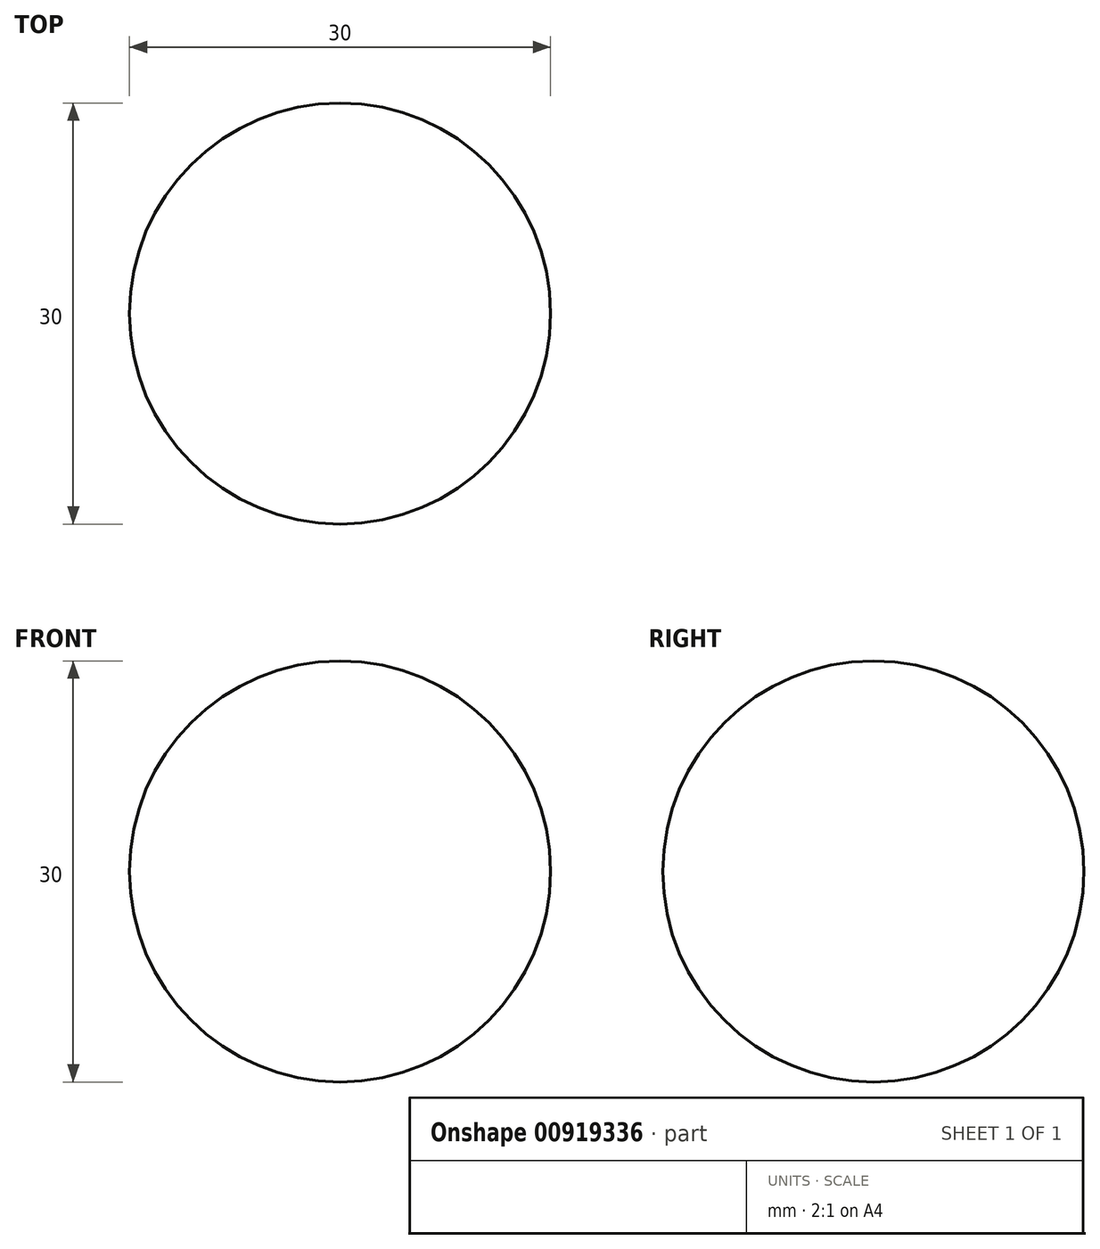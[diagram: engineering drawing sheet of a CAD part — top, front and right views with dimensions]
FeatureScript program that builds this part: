
annotation { "Feature Type Name" : "Feature", "Feature Type Description" : "" }
export const myFeature = defineFeature(function(context is Context, id is Id, definition is map)
    precondition{}
    {
        {
            var Q0;
            Q0=qCreatedBy(makeId("Top.planeOp"),FACE);
            var sketch = newSketch(context, id + "F0", { "sketchPlane" : qUnion([Q0])});
            skCircle(sketch, "E0", {"center": v(0, 0) * mm, "radius": 15 * mm});
            skLineSegment(sketch, "E1", {"start": v(0, 15) * mm, "end": v(0, -15) * mm});
            skSolve(sketch);
        }
        {
            var Q0;
            {var subQ0=sQuery(id+"F0.wireOp",EDGE,"E1");Q0=makeQuery(id+"F0.imprint","IMPRINT",FACE,{"disambiguationData":[TD([[makeQuery(id+"F0.imprint","IMPRINT",EDGE,{"derivedFrom":subQ0}),1.0]])]});}
            var Q1;
            Q1=sQuery(id+"F0.wireOp",EDGE,"E1");
            revolve(context, id + "F1", {"surfaceOperationType" : NewSurfaceOperationType.NEW, "entities" : qUnion([Q0]), "axis" : qUnion([Q1]), "revolveType" : RevolveType.FULL});
        }
    });
